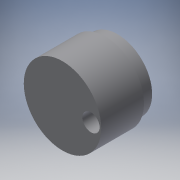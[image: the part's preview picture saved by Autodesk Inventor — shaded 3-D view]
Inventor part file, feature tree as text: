
AUTODESK INVENTOR PART (.ipt)
format: ipt  version: 2016 (Build 200138000, 138)  size: 116,736 bytes
history: native  units: in
note: dims shown in document units (in); Inventor stores cm internally (conversion verified against a paired STEP export)
features: extrude x4, sketch x3, reference x2
ambient origin geometry x8: Origin, YZ Plane, XZ Plane, XY Plane, X Axis, Y Axis, Z Axis, Center Point
bodies: Solid1 (feature_tree)
feature tree (9):
  extrude  "Extrusion1"  Depth=0.4134in TaperAngle=0.0deg
  extrude  "Extrusion2"  Depth=0.1673in
  extrude  "Extrusion3"  Depth=0.3937in
  extrude  "Extrusion5"  Depth=0.1181in TaperAngle=0.0deg
  reference  "Reference1"
  sketch  "Sketch2"  dims[d0=0.748in d1=0.4134in d2=0.0in]
  sketch  "Sketch3"  dims[d3=0.0984in d4=0.1673in]
  reference  "Reference2"
  sketch  "Sketch5"  dims[d5=0.1969in d6=0.0in d7=0.6693in d8=0.1181in d9=0.0in d13=0.0787in d14=0.3937in d15=0.0in]
